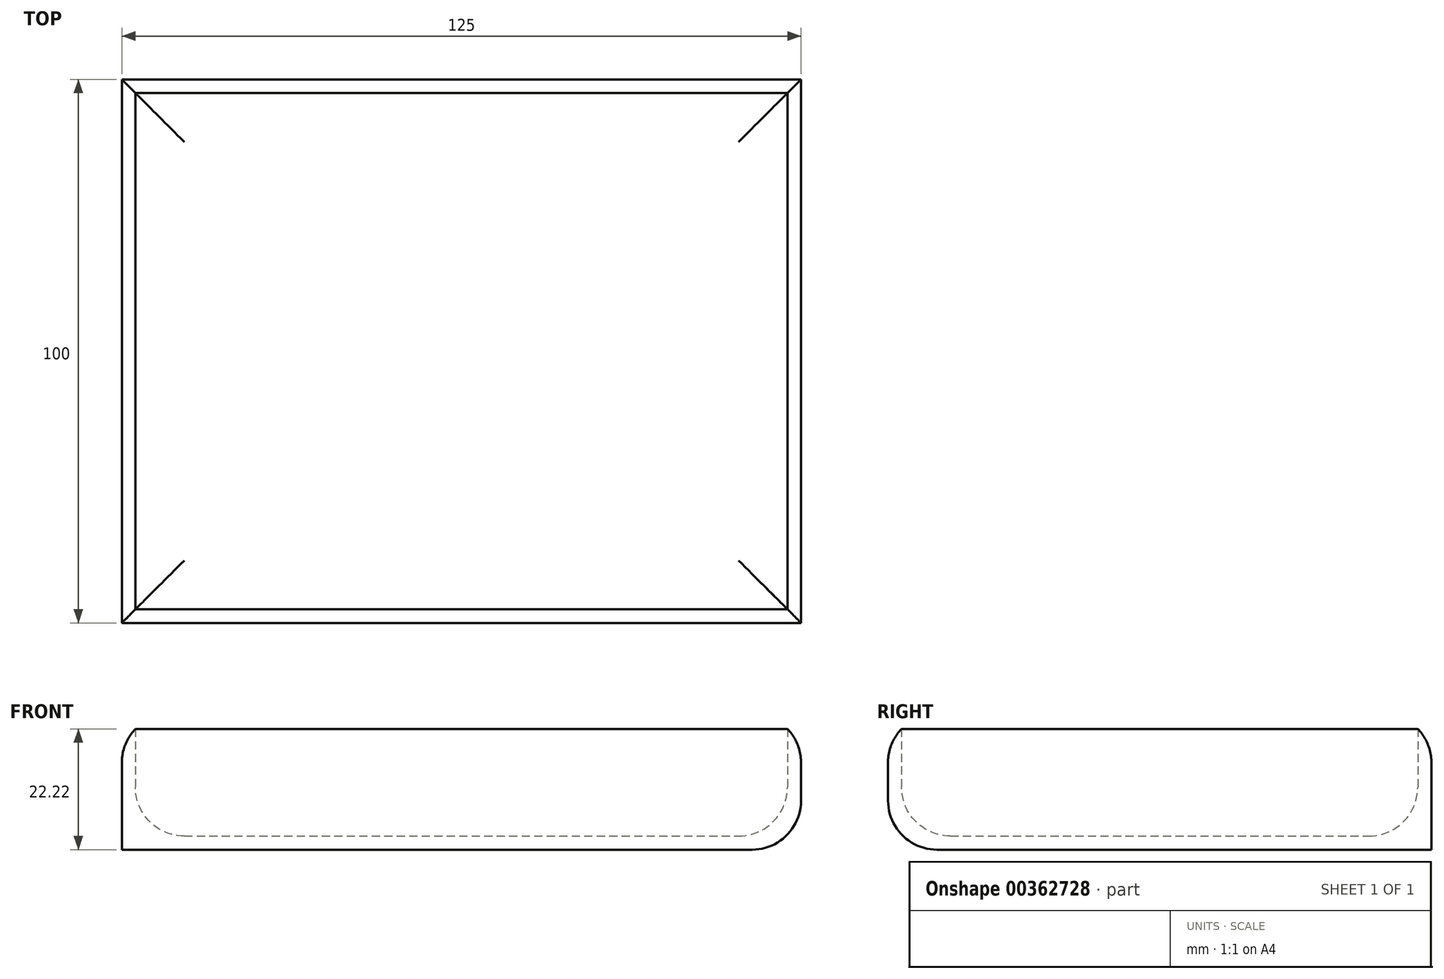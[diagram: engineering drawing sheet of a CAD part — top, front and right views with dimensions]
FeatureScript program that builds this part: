
annotation { "Feature Type Name" : "Feature", "Feature Type Description" : "" }
export const myFeature = defineFeature(function(context is Context, id is Id, definition is map)
    precondition{}
    {
        {
            var Q0;
            Q0=qCreatedBy(makeId("Top.planeOp"),FACE);
            var sketch = newSketch(context, id + "F0", { "sketchPlane" : qUnion([Q0])});
            skLineSegment(sketch, "E0.bottom", {"start": v(0, 0) * mm, "end": v(125, 0) * mm});
            skLineSegment(sketch, "E0.top", {"start": v(0, 100) * mm, "end": v(125, 100) * mm});
            skLineSegment(sketch, "E0.left", {"start": v(0, 0) * mm, "end": v(0, 100) * mm});
            skLineSegment(sketch, "E0.right", {"start": v(125, 0) * mm, "end": v(125, 100) * mm});
            skSolve(sketch);
        }
        {
            var Q0;
            Q0=makeQuery(id+"F0.imprint","IMPRINT",FACE,{"disambiguationData":[TD([[makeQuery(id+"F0.imprint","IMPRINT",EDGE,{"derivedFrom":sQuery(id+"F0.wireOp",EDGE,"E0.bottom")}),1.0]])]});
            extrude(context, id + "F1", {"entities" : qUnion([Q0]), "depth" : 25 * mm});
        }
        {
            var Q0;
            Q0=makeQuery(id+"F1.opExtrude","CAP_FACE",FACE,{"disambiguationData":[OSD([sQuery(id+"F0.wireOp",EDGE,"E0.bottom"),sQuery(id+"F0.wireOp",EDGE,"E0.top"),sQuery(id+"F0.wireOp",EDGE,"E0.left"),sQuery(id+"F0.wireOp",EDGE,"E0.right")])],"isStart":false});
            shell(context, id + "F2", {"entities" : qUnion([Q0]), "thickness" : 2.5 * mm});
        }
        {
            var Q0;
            Q0=makeQuery(id+"F1.opExtrude","CAP_EDGE",EDGE,{"disambiguationData":[OSD([sQuery(id+"F0.wireOp",EDGE,"E0.bottom")])],"isStart":false});
            var Q1;
            Q1=makeQuery(id+"F1.opExtrude","CAP_EDGE",EDGE,{"disambiguationData":[OSD([sQuery(id+"F0.wireOp",EDGE,"E0.bottom")])],"isStart":true});
            var Q2;
            Q2=makeQuery(id+"F1.opExtrude","CAP_EDGE",EDGE,{"disambiguationData":[OSD([sQuery(id+"F0.wireOp",EDGE,"E0.right")])],"isStart":true});
            var Q3;
            Q3=makeQuery(id+"F2.opShell","OFFSET_FACE",FACE,{"disambiguationData":[OSD([sQuery(id+"F0.wireOp",EDGE,"E0.bottom"),sQuery(id+"F0.wireOp",EDGE,"E0.top"),sQuery(id+"F0.wireOp",EDGE,"E0.left"),sQuery(id+"F0.wireOp",EDGE,"E0.right")])]});
            var Q4;
            Q4=makeQuery(id+"F1.opExtrude","CAP_EDGE",EDGE,{"disambiguationData":[OSD([sQuery(id+"F0.wireOp",EDGE,"E0.right")])],"isStart":false});
            var Q5;
            Q5=makeQuery(id+"F1.opExtrude","CAP_EDGE",EDGE,{"disambiguationData":[OSD([sQuery(id+"F0.wireOp",EDGE,"E0.top")])],"isStart":false});
            var Q6;
            Q6=makeQuery(id+"F1.opExtrude","CAP_EDGE",EDGE,{"disambiguationData":[OSD([sQuery(id+"F0.wireOp",EDGE,"E0.left")])],"isStart":false});
            fillet(context, id + "F3", {"entities" : qUnion([Q0, Q1, Q2, Q3, Q4, Q5, Q6]), "radius" : 9 * mm, "tangentPropagation" : true, "allowEdgeOverflow" : false});
        }
    });
